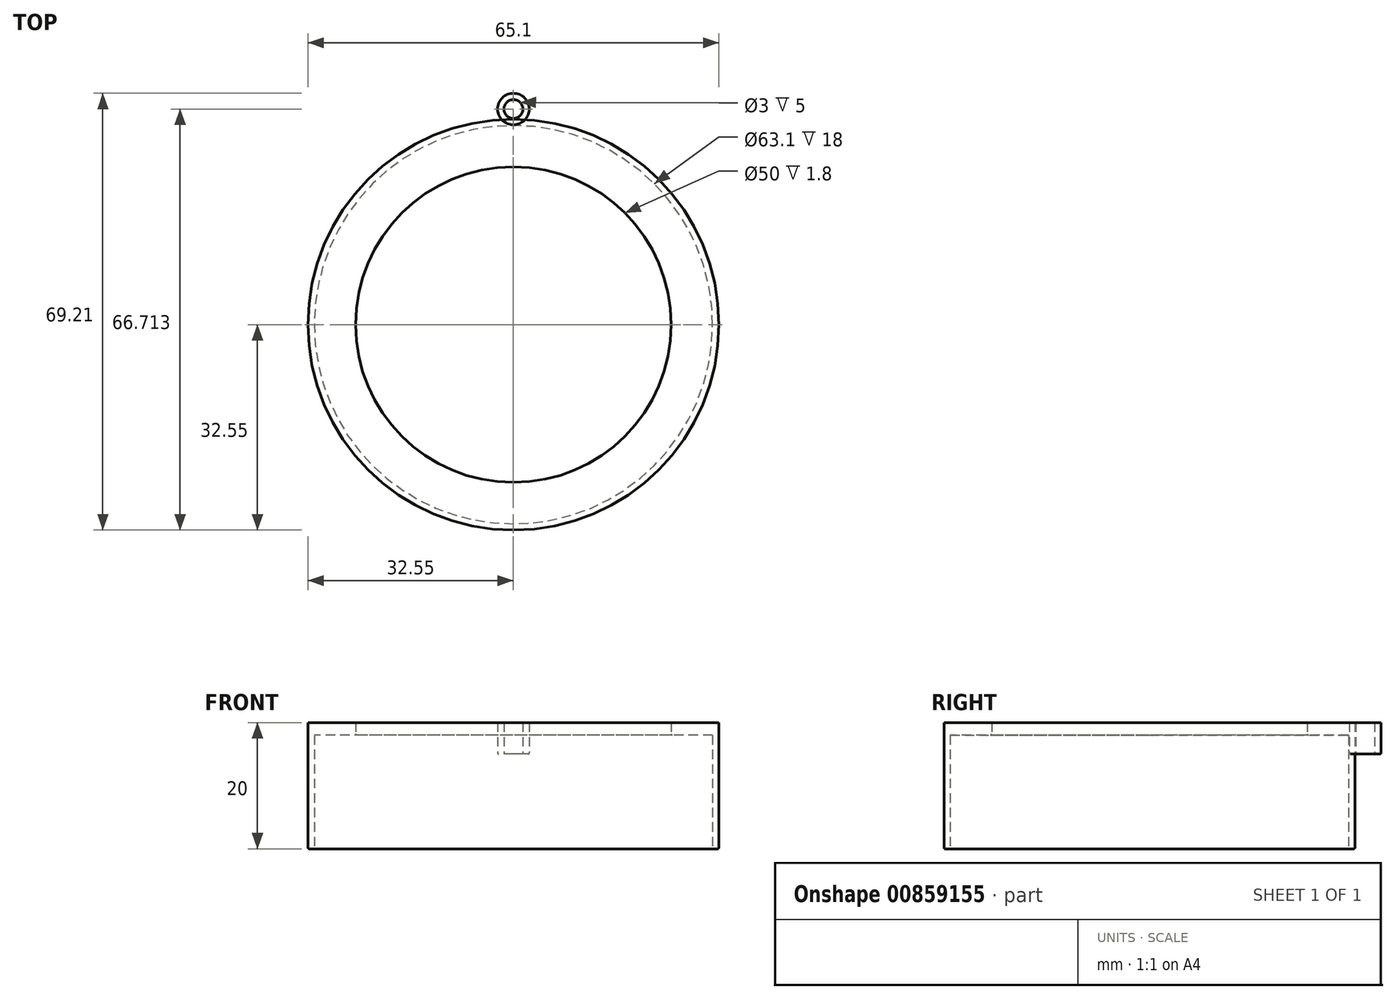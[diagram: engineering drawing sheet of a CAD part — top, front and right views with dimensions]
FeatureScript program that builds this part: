
annotation { "Feature Type Name" : "Feature", "Feature Type Description" : "" }
export const myFeature = defineFeature(function(context is Context, id is Id, definition is map)
    precondition{}
    {
        {
            var Q0;
            Q0=qCreatedBy(makeId("Top.planeOp"),FACE);
            var sketch = newSketch(context, id + "F0", { "sketchPlane" : qUnion([Q0])});
            skCircle(sketch, "E0", {"center": v(0, 0) * mm, "radius": 32.55 * mm});
            skSolve(sketch);
        }
        {
            var Q0;
            Q0=makeQuery(id+"F0.imprint","IMPRINT",FACE,{"disambiguationData":[TD([[makeQuery(id+"F0.imprint","IMPRINT",EDGE,{"derivedFrom":sQuery(id+"F0.wireOp",EDGE,"E0")}),1.0]])]});
            extrude(context, id + "F1", {"entities" : qUnion([Q0]), "depth" : 20 * mm, "offsetDistance" : 25.4 * mm});
        }
        {
            var Q0;
            Q0=qCreatedBy(makeId("Top.planeOp"),FACE);
            var sketch = newSketch(context, id + "F2", { "sketchPlane" : qUnion([Q0])});
            skCircle(sketch, "E1", {"center": v(0, 0) * mm, "radius": 31.55 * mm});
            skSolve(sketch);
        }
        {
            var Q0;
            Q0 = qSketchRegion(id + "F2", true);
            extrude(context, id + "F3", {"entities" : qUnion([Q0]), "operationType" : NewBodyOperationType.REMOVE, "depth" : 18 * mm, "offsetDistance" : 25.4 * mm});
        }
        {
            var Q0;
            Q0=qCreatedBy(makeId("Top.planeOp"),FACE);
            var sketch = newSketch(context, id + "F4", { "sketchPlane" : qUnion([Q0])});
            skCircle(sketch, "E2", {"center": v(0, 0) * mm, "radius": 25 * mm});
            skSolve(sketch);
        }
        {
            var Q0;
            Q0=makeQuery(id+"F4.imprint","IMPRINT",FACE,{"disambiguationData":[TD([[makeQuery(id+"F4.imprint","IMPRINT",EDGE,{"derivedFrom":sQuery(id+"F4.wireOp",EDGE,"E2")}),1.0]])]});
            extrude(context, id + "F5", {"entities" : qUnion([Q0]), "operationType" : NewBodyOperationType.REMOVE, "depth" : 20 * mm, "offsetDistance" : 25.4 * mm});
        }
        {
            var Q0;
            Q0=qCreatedBy(makeId("Top.planeOp"),FACE);
            var sketch = newSketch(context, id + "F6", { "sketchPlane" : qUnion([Q0])});
            skCircle(sketch, "E3", {"center": v(0, 0) * mm, "radius": 2.5 * mm});
            skSolve(sketch);
        }
        {
            var Q0;
            Q0 = qSketchRegion(id + "F6", true);
            extrude(context, id + "F7", {"entities" : qUnion([Q0]), "depth" : 5 * mm, "offsetDistance" : 25.4 * mm});
        }
        {
            var Q0;
            Q0=qCreatedBy(makeId("Top.planeOp"),FACE);
            var sketch = newSketch(context, id + "F8", { "sketchPlane" : qUnion([Q0])});
            skCircle(sketch, "E4", {"center": v(0, 0) * mm, "radius": 1.5 * mm});
            skSolve(sketch);
        }
        {
            var Q0;
            Q0 = qSketchRegion(id + "F8", true);
            extrude(context, id + "F9", {"entities" : qUnion([Q0]), "operationType" : NewBodyOperationType.REMOVE, "depth" : 5 * mm, "offsetDistance" : 25.4 * mm});
        }
        {
            var Q0;
            Q0=makeQuery(id+"F7.opExtrude","SWEPT_BODY",BODY,{"disambiguationData":[OSD([sQuery(id+"F6.wireOp",EDGE,"E3")])]});
            transform(context, id + "F10", {"entities" : qUnion([Q0]), "transformType" : TransformType.TRANSLATION_3D, "dx" : 0 * mm, "dy" : 33.78 * mm, "dz" : 15 * mm, "makeCopy" : false});
        }
        {
            var Q0;
            Q0=makeQuery(id+"F9.boolean.opBoolean","COPY",EDGE,{"derivedFrom":makeQuery(id+"F9.opExtrude","CAP_EDGE",EDGE,{"disambiguationData":[OSD([sQuery(id+"F8.wireOp",EDGE,"E4")])],"isStart":true})});
            var Q1;
            {var subQ0=sQuery(id+"F6.wireOp",EDGE,"E3");Q1=makeQuery(id+"FQi8ywXzMQbMwHG_2.opBoolean","SPLIT",EDGE,{"disambiguationData":[TD([makeQuery(id+"F1.opExtrude","SWEPT_FACE",FACE,{"disambiguationData":[OSD([sQuery(id+"F0.wireOp",EDGE,"E0")])]})])],"derivedFrom":makeQuery(id+"F7.opExtrude","CAP_EDGE",EDGE,{"disambiguationData":[OSD([subQ0])],"isStart":true})});}
            var Q2;
            Q2=makeQuery(id+"F1.opExtrude","CAP_EDGE",EDGE,{"disambiguationData":[OSD([sQuery(id+"F0.wireOp",EDGE,"E0")])],"isStart":true});
            var Q3;
            Q3=makeQuery(id+"F3.boolean.opBoolean","COPY",EDGE,{"derivedFrom":makeQuery(id+"F3.opExtrude","CAP_EDGE",EDGE,{"disambiguationData":[OSD([sQuery(id+"F2.wireOp",EDGE,"E1")])],"isStart":true})});
            var Q4;
            Q4=makeQuery(id+"F5.boolean.opBoolean","INTERSECT",EDGE,{"derivedFrom":[makeQuery(id+"F3.boolean.opBoolean","COPY",FACE,{"derivedFrom":makeQuery(id+"F3.opExtrude","CAP_FACE",FACE,{"disambiguationData":[OSD([sQuery(id+"F2.wireOp",EDGE,"E1")])],"isStart":false})}),makeQuery(id+"F5.opExtrude","SWEPT_FACE",FACE,{"disambiguationData":[OSD([sQuery(id+"F4.wireOp",EDGE,"E2")])]})]});
            fillet(context, id + "F11", {"entities" : qUnion([Q0, Q1, Q2, Q3, Q4]), "radius" : 0.2 * mm, "tangentPropagation" : true, "allowEdgeOverflow" : false});
        }
        {
            var Q0;
            Q0=makeQuery(id+"F7.opExtrude","SWEPT_BODY",BODY,{"disambiguationData":[OSD([sQuery(id+"F6.wireOp",EDGE,"E3")])]});
            transform(context, id + "F12", {"entities" : qUnion([Q0]), "transformType" : TransformType.TRANSLATION_3D, "dx" : 0 * mm, "dy" : 0.25 * mm, "dz" : 0 * mm, "makeCopy" : false});
        }
        {
            var Q0;
            Q0=makeQuery(id+"F7.opExtrude","SWEPT_BODY",BODY,{"disambiguationData":[OSD([sQuery(id+"F6.wireOp",EDGE,"E3")])]});
            transform(context, id + "F13", {"entities" : qUnion([Q0]), "transformType" : TransformType.TRANSLATION_3D, "dx" : 0 * mm, "dy" : 0.13 * mm, "dz" : 0 * mm, "makeCopy" : false});
        }
    });
